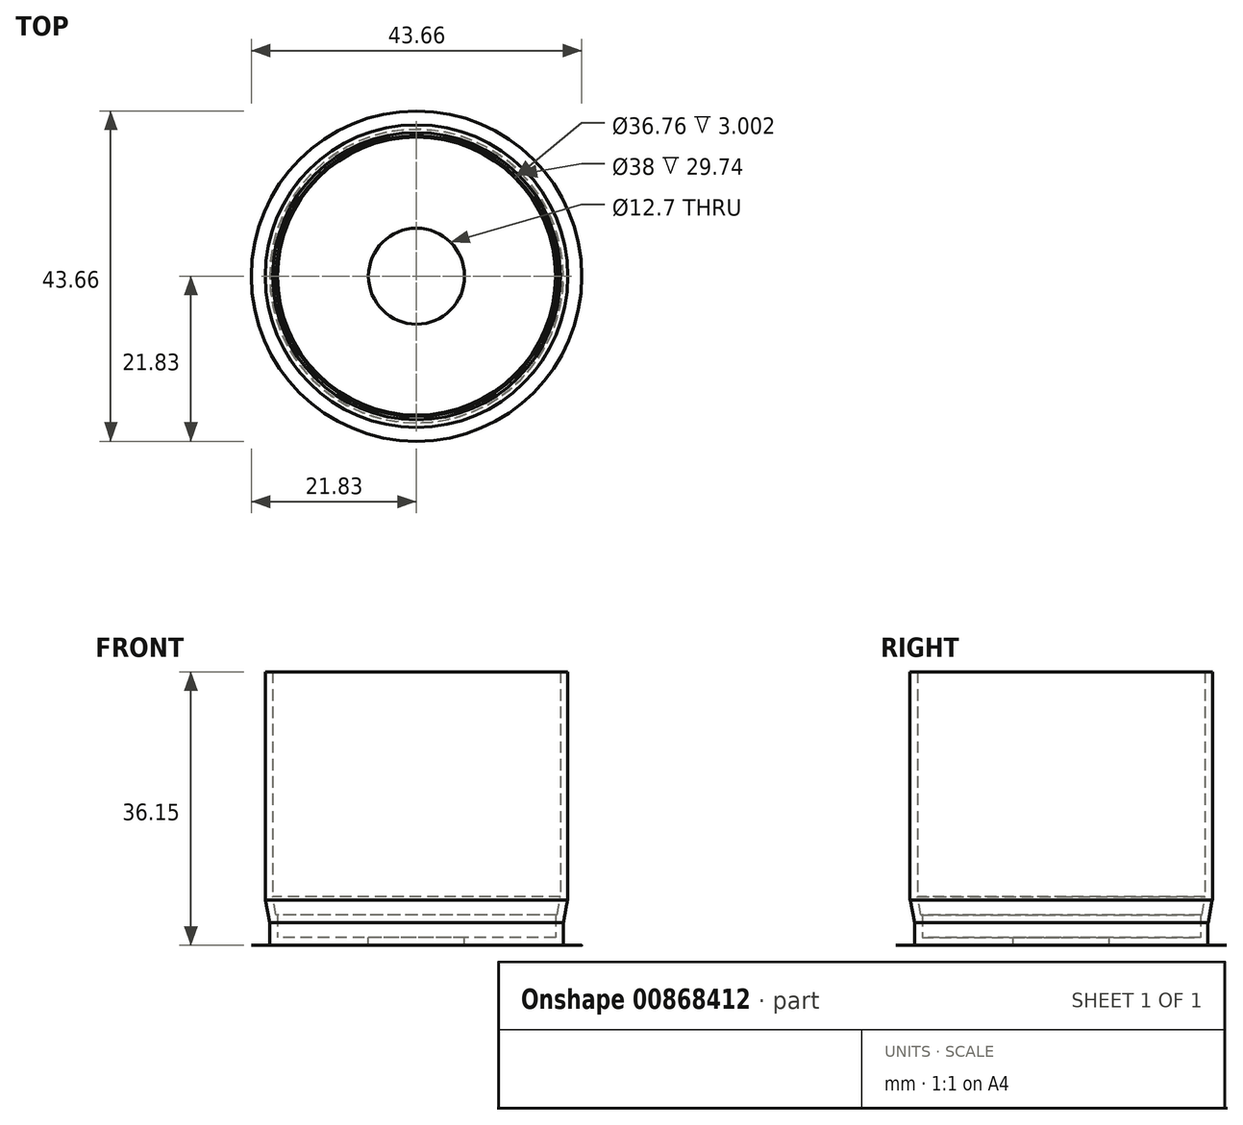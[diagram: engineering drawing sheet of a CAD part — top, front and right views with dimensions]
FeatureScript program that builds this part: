
annotation { "Feature Type Name" : "Feature", "Feature Type Description" : "" }
export const myFeature = defineFeature(function(context is Context, id is Id, definition is map)
    precondition{}
    {
        {
            var Q0;
            Q0=qCreatedBy(makeId("Top.planeOp"),FACE);
            var sketch = newSketch(context, id + "F0", { "sketchPlane" : qUnion([Q0])});
            skCircle(sketch, "E0", {"center": v(0, 0) * mm, "radius": 21.83 * mm});
            skSolve(sketch);
        }
        {
            var Q0;
            Q0 = qSketchRegion(id + "F0", true);
            extrude(context, id + "F1", {"entities" : qUnion([Q0]), "depth" : 1 / 406.4 * mm, "offsetDistance" : 25.4 * mm});
        }
        {
            var Q0;
            Q0=makeQuery(id+"F1.opExtrude","CAP_FACE",FACE,{"disambiguationData":[OSD([sQuery(id+"F0.wireOp",EDGE,"E0")])],"isStart":false});
            var sketch = newSketch(context, id + "F2", { "sketchPlane" : qUnion([Q0])});
            skCircle(sketch, "E1", {"center": v(0, 0) * mm, "radius": 19.38 * mm});
            skSolve(sketch);
        }
        {
            var Q0;
            Q0 = qSketchRegion(id + "F2", true);
            extrude(context, id + "F3", {"entities" : qUnion([Q0]), "operationType" : NewBodyOperationType.ADD, "depth" : 3 * mm, "offsetDistance" : 25.4 * mm});
        }
        {
            var Q0;
            Q0=makeQuery(id+"F3.opExtrude","CAP_FACE",FACE,{"disambiguationData":[OSD([sQuery(id+"F2.wireOp",EDGE,"E1")])],"isStart":false});
            var sketch = newSketch(context, id + "F4", { "sketchPlane" : qUnion([Q0])});
            skCircle(sketch, "E2", {"center": v(0, 0) * mm, "radius": 19.41 * mm});
            skSolve(sketch);
        }
        {
            var Q0;
            Q0 = qSketchRegion(id + "F4", true);
            extrude(context, id + "F5", {"entities" : qUnion([Q0]), "operationType" : NewBodyOperationType.ADD, "depth" : 3 * mm, "offsetDistance" : 25.4 * mm, "hasDraft" : true, "draftAngle" : 10 * degree});
        }
        {
            var Q0;
            Q0=makeQuery(id+"F5.opExtrude","CAP_FACE",FACE,{"disambiguationData":[OSD([sQuery(id+"F4.wireOp",EDGE,"E2")])],"isStart":false});
            var sketch = newSketch(context, id + "F6", { "sketchPlane" : qUnion([Q0])});
            skCircle(sketch, "E3", {"center": v(0, 0) * mm, "radius": 20 * mm});
            skSolve(sketch);
        }
        {
            var Q0;
            Q0 = qSketchRegion(id + "F6", true);
            extrude(context, id + "F7", {"entities" : qUnion([Q0]), "operationType" : NewBodyOperationType.ADD, "depth" : 30.15 * mm, "offsetDistance" : 25.4 * mm});
        }
        {
            var Q0;
            Q0=makeQuery(id+"F7.opExtrude","CAP_FACE",FACE,{"disambiguationData":[OSD([sQuery(id+"F6.wireOp",EDGE,"E3")])],"isStart":false});
            shell(context, id + "F8", {"entities" : qUnion([Q0]), "thickness" : 1 * mm});
        }
        {
            var Q0;
            Q0=makeQuery(id+"F1.opExtrude","CAP_FACE",FACE,{"disambiguationData":[OSD([sQuery(id+"F0.wireOp",EDGE,"E0")])],"isStart":true});
            var sketch = newSketch(context, id + "F9", { "sketchPlane" : qUnion([Q0])});
            skCircle(sketch, "E4", {"center": v(0, 0) * mm, "radius": 6.6 * mm});
            skSolve(sketch);
        }
        {
            var Q0;
            Q0=sQuery(id+"F9.wireOp",VERTEX,"E4.center");
            var Q1;
            Q1=makeQuery(id+"F1.opExtrude","SWEPT_BODY",BODY,{"disambiguationData":[OSD([sQuery(id+"F0.wireOp",EDGE,"E0")])]});
            hole(context, id + "F10", {"style" : HoleStyle.SIMPLE, "endStyle" : HoleEndStyle.THROUGH, "holeDiameter" : 12.7 * mm, "majorDiameter" : 19.05 * mm, "isTappedThrough" : true, "tappedDepth" : 76.2 * mm, "tapClearance" : 3, "startFromSketch" : true, "locations" : qUnion([Q0]), "scope" : qUnion([Q1])});
        }
    });
